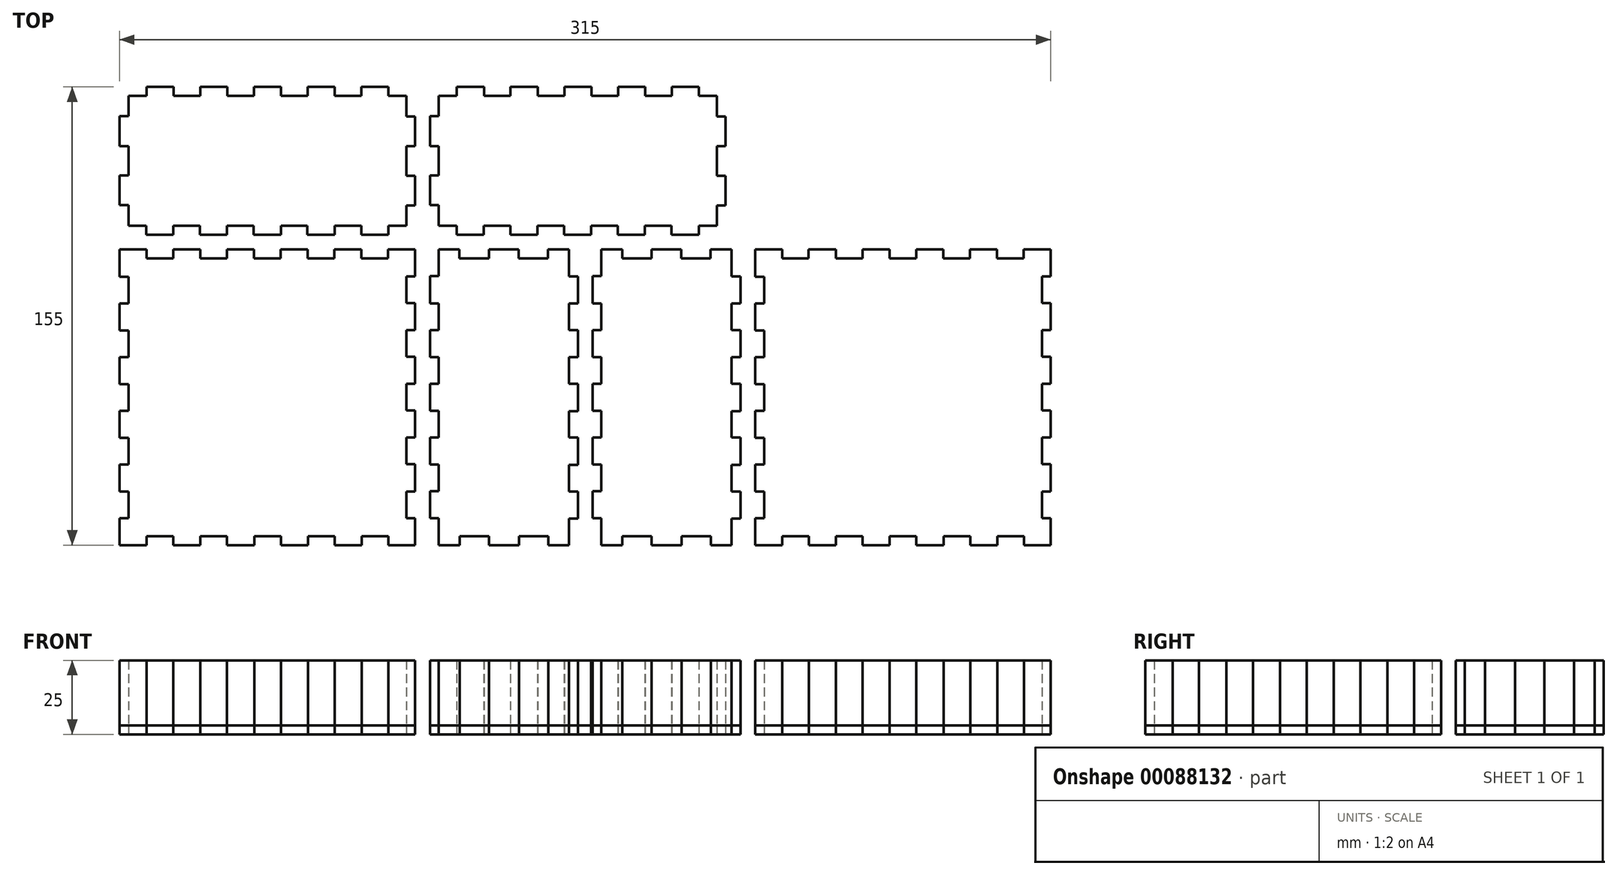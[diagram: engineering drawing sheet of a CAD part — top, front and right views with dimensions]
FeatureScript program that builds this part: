
annotation { "Feature Type Name" : "Feature", "Feature Type Description" : "" }
export const myFeature = defineFeature(function(context is Context, id is Id, definition is map)
    precondition{}
    {
        {
            var Q0;
            Q0=qCreatedBy(makeId("Top.planeOp"),FACE);
            var sketch = newSketch(context, id + "F0", { "sketchPlane" : qUnion([Q0])});
            skLineSegment(sketch, "E0", {"start": v(-154.5, -68.4) * mm, "end": v(-157.5, -68.4) * mm});
            skLineSegment(sketch, "E1", {"start": v(-157.5, -68.4) * mm, "end": v(-157.5, -77.5) * mm});
            skLineSegment(sketch, "E2", {"start": v(-157.5, -77.5) * mm, "end": v(-148.33, -77.5) * mm});
            skLineSegment(sketch, "E3", {"start": v(-148.33, -77.5) * mm, "end": v(-148.33, -74.5) * mm});
            skLineSegment(sketch, "E4", {"start": v(-148.33, -74.5) * mm, "end": v(-139.32, -74.5) * mm});
            skLineSegment(sketch, "E5", {"start": v(-139.32, -74.5) * mm, "end": v(-139.32, -77.5) * mm});
            skLineSegment(sketch, "E6", {"start": v(-139.32, -77.5) * mm, "end": v(-130.15, -77.5) * mm});
            skLineSegment(sketch, "E7", {"start": v(-130.15, -77.5) * mm, "end": v(-130.15, -74.5) * mm});
            skLineSegment(sketch, "E8", {"start": v(-130.15, -74.5) * mm, "end": v(-121.14, -74.5) * mm});
            skLineSegment(sketch, "E9", {"start": v(-121.14, -74.5) * mm, "end": v(-121.14, -77.5) * mm});
            skLineSegment(sketch, "E10", {"start": v(-121.14, -77.5) * mm, "end": v(-111.97, -77.5) * mm});
            skLineSegment(sketch, "E11", {"start": v(-111.97, -77.5) * mm, "end": v(-111.97, -74.5) * mm});
            skLineSegment(sketch, "E12", {"start": v(-111.97, -74.5) * mm, "end": v(-102.95, -74.5) * mm});
            skLineSegment(sketch, "E13", {"start": v(-102.95, -74.5) * mm, "end": v(-102.95, -77.5) * mm});
            skLineSegment(sketch, "E14", {"start": v(-102.95, -77.5) * mm, "end": v(-93.78, -77.5) * mm});
            skLineSegment(sketch, "E15", {"start": v(-93.78, -77.5) * mm, "end": v(-93.78, -74.5) * mm});
            skLineSegment(sketch, "E16", {"start": v(-93.78, -74.5) * mm, "end": v(-84.77, -74.5) * mm});
            skLineSegment(sketch, "E17", {"start": v(-84.77, -74.5) * mm, "end": v(-84.77, -77.5) * mm});
            skLineSegment(sketch, "E18", {"start": v(-84.77, -77.5) * mm, "end": v(-75.6, -77.5) * mm});
            skLineSegment(sketch, "E19", {"start": v(-75.6, -77.5) * mm, "end": v(-75.6, -74.5) * mm});
            skLineSegment(sketch, "E20", {"start": v(-75.6, -74.5) * mm, "end": v(-66.6, -74.5) * mm});
            skLineSegment(sketch, "E21", {"start": v(-66.6, -74.5) * mm, "end": v(-66.6, -77.5) * mm});
            skLineSegment(sketch, "E22", {"start": v(-66.6, -77.5) * mm, "end": v(-57.5, -77.5) * mm});
            skLineSegment(sketch, "E23", {"start": v(-57.5, -77.5) * mm, "end": v(-57.5, -68.33) * mm});
            skLineSegment(sketch, "E24", {"start": v(-57.5, -68.33) * mm, "end": v(-60.5, -68.33) * mm});
            skLineSegment(sketch, "E25", {"start": v(-60.5, -68.33) * mm, "end": v(-60.5, -59.32) * mm});
            skLineSegment(sketch, "E26", {"start": v(-60.5, -59.32) * mm, "end": v(-57.5, -59.32) * mm});
            skLineSegment(sketch, "E27", {"start": v(-57.5, -59.32) * mm, "end": v(-57.5, -50.15) * mm});
            skLineSegment(sketch, "E28", {"start": v(-57.5, -50.15) * mm, "end": v(-60.5, -50.15) * mm});
            skLineSegment(sketch, "E29", {"start": v(-60.5, -50.15) * mm, "end": v(-60.5, -41.14) * mm});
            skLineSegment(sketch, "E30", {"start": v(-60.5, -41.14) * mm, "end": v(-57.5, -41.14) * mm});
            skLineSegment(sketch, "E31", {"start": v(-57.5, -41.14) * mm, "end": v(-57.5, -31.97) * mm});
            skLineSegment(sketch, "E32", {"start": v(-57.5, -31.97) * mm, "end": v(-60.5, -31.97) * mm});
            skLineSegment(sketch, "E33", {"start": v(-60.5, -31.97) * mm, "end": v(-60.5, -22.95) * mm});
            skLineSegment(sketch, "E34", {"start": v(-60.5, -22.95) * mm, "end": v(-57.5, -22.95) * mm});
            skLineSegment(sketch, "E35", {"start": v(-57.5, -22.95) * mm, "end": v(-57.5, -13.78) * mm});
            skLineSegment(sketch, "E36", {"start": v(-57.5, -13.78) * mm, "end": v(-60.5, -13.78) * mm});
            skLineSegment(sketch, "E37", {"start": v(-60.5, -13.78) * mm, "end": v(-60.5, -4.77) * mm});
            skLineSegment(sketch, "E38", {"start": v(-60.5, -4.77) * mm, "end": v(-57.5, -4.77) * mm});
            skLineSegment(sketch, "E39", {"start": v(-57.5, -4.77) * mm, "end": v(-57.5, 4.4) * mm});
            skLineSegment(sketch, "E40", {"start": v(-57.5, 4.4) * mm, "end": v(-60.5, 4.4) * mm});
            skLineSegment(sketch, "E41", {"start": v(-60.5, 4.4) * mm, "end": v(-60.5, 13.4) * mm});
            skLineSegment(sketch, "E42", {"start": v(-60.5, 13.4) * mm, "end": v(-57.5, 13.4) * mm});
            skLineSegment(sketch, "E43", {"start": v(-57.5, 13.4) * mm, "end": v(-57.5, 22.5) * mm});
            skLineSegment(sketch, "E44", {"start": v(-57.5, 22.5) * mm, "end": v(-66.67, 22.5) * mm});
            skLineSegment(sketch, "E45", {"start": v(-66.67, 22.5) * mm, "end": v(-66.67, 19.5) * mm});
            skLineSegment(sketch, "E46", {"start": v(-66.67, 19.5) * mm, "end": v(-75.68, 19.5) * mm});
            skLineSegment(sketch, "E47", {"start": v(-75.68, 19.5) * mm, "end": v(-75.68, 22.5) * mm});
            skLineSegment(sketch, "E48", {"start": v(-75.68, 22.5) * mm, "end": v(-84.85, 22.5) * mm});
            skLineSegment(sketch, "E49", {"start": v(-84.85, 22.5) * mm, "end": v(-84.85, 19.5) * mm});
            skLineSegment(sketch, "E50", {"start": v(-84.85, 19.5) * mm, "end": v(-93.86, 19.5) * mm});
            skLineSegment(sketch, "E51", {"start": v(-93.86, 19.5) * mm, "end": v(-93.86, 22.5) * mm});
            skLineSegment(sketch, "E52", {"start": v(-93.86, 22.5) * mm, "end": v(-103.03, 22.5) * mm});
            skLineSegment(sketch, "E53", {"start": v(-103.03, 22.5) * mm, "end": v(-103.03, 19.5) * mm});
            skLineSegment(sketch, "E54", {"start": v(-103.03, 19.5) * mm, "end": v(-112.05, 19.5) * mm});
            skLineSegment(sketch, "E55", {"start": v(-112.05, 19.5) * mm, "end": v(-112.05, 22.5) * mm});
            skLineSegment(sketch, "E56", {"start": v(-112.05, 22.5) * mm, "end": v(-121.22, 22.5) * mm});
            skLineSegment(sketch, "E57", {"start": v(-121.22, 22.5) * mm, "end": v(-121.22, 19.5) * mm});
            skLineSegment(sketch, "E58", {"start": v(-121.22, 19.5) * mm, "end": v(-130.23, 19.5) * mm});
            skLineSegment(sketch, "E59", {"start": v(-130.23, 19.5) * mm, "end": v(-130.23, 22.5) * mm});
            skLineSegment(sketch, "E60", {"start": v(-130.23, 22.5) * mm, "end": v(-139.4, 22.5) * mm});
            skLineSegment(sketch, "E61", {"start": v(-139.4, 22.5) * mm, "end": v(-139.4, 19.5) * mm});
            skLineSegment(sketch, "E62", {"start": v(-139.4, 19.5) * mm, "end": v(-148.4, 19.5) * mm});
            skLineSegment(sketch, "E63", {"start": v(-148.4, 19.5) * mm, "end": v(-148.4, 22.5) * mm});
            skLineSegment(sketch, "E64", {"start": v(-148.4, 22.5) * mm, "end": v(-157.5, 22.5) * mm});
            skLineSegment(sketch, "E65", {"start": v(-157.5, 22.5) * mm, "end": v(-157.5, 13.33) * mm});
            skLineSegment(sketch, "E66", {"start": v(-157.5, 13.33) * mm, "end": v(-154.5, 13.33) * mm});
            skLineSegment(sketch, "E67", {"start": v(-154.5, 13.33) * mm, "end": v(-154.5, 4.32) * mm});
            skLineSegment(sketch, "E68", {"start": v(-154.5, 4.32) * mm, "end": v(-157.5, 4.32) * mm});
            skLineSegment(sketch, "E69", {"start": v(-157.5, 4.32) * mm, "end": v(-157.5, -4.85) * mm});
            skLineSegment(sketch, "E70", {"start": v(-157.5, -4.85) * mm, "end": v(-154.5, -4.85) * mm});
            skLineSegment(sketch, "E71", {"start": v(-154.5, -4.85) * mm, "end": v(-154.5, -13.86) * mm});
            skLineSegment(sketch, "E72", {"start": v(-154.5, -13.86) * mm, "end": v(-157.5, -13.86) * mm});
            skLineSegment(sketch, "E73", {"start": v(-157.5, -13.86) * mm, "end": v(-157.5, -23.03) * mm});
            skLineSegment(sketch, "E74", {"start": v(-157.5, -23.03) * mm, "end": v(-154.5, -23.03) * mm});
            skLineSegment(sketch, "E75", {"start": v(-154.5, -23.03) * mm, "end": v(-154.5, -32.05) * mm});
            skLineSegment(sketch, "E76", {"start": v(-154.5, -32.05) * mm, "end": v(-157.5, -32.05) * mm});
            skLineSegment(sketch, "E77", {"start": v(-157.5, -32.05) * mm, "end": v(-157.5, -41.22) * mm});
            skLineSegment(sketch, "E78", {"start": v(-157.5, -41.22) * mm, "end": v(-154.5, -41.22) * mm});
            skLineSegment(sketch, "E79", {"start": v(-154.5, -41.22) * mm, "end": v(-154.5, -50.23) * mm});
            skLineSegment(sketch, "E80", {"start": v(-154.5, -50.23) * mm, "end": v(-157.5, -50.23) * mm});
            skLineSegment(sketch, "E81", {"start": v(-157.5, -50.23) * mm, "end": v(-157.5, -59.4) * mm});
            skLineSegment(sketch, "E82", {"start": v(-157.5, -59.4) * mm, "end": v(-154.5, -59.4) * mm});
            skLineSegment(sketch, "E83", {"start": v(-154.5, -59.4) * mm, "end": v(-154.5, -68.4) * mm});
            skLineSegment(sketch, "E84", {"start": v(60.5, -68.4) * mm, "end": v(57.5, -68.4) * mm});
            skLineSegment(sketch, "E85", {"start": v(57.5, -68.4) * mm, "end": v(57.5, -77.5) * mm});
            skLineSegment(sketch, "E86", {"start": v(57.5, -77.5) * mm, "end": v(66.67, -77.5) * mm});
            skLineSegment(sketch, "E87", {"start": v(66.67, -77.5) * mm, "end": v(66.67, -74.5) * mm});
            skLineSegment(sketch, "E88", {"start": v(66.67, -74.5) * mm, "end": v(75.68, -74.5) * mm});
            skLineSegment(sketch, "E89", {"start": v(75.68, -74.5) * mm, "end": v(75.68, -77.5) * mm});
            skLineSegment(sketch, "E90", {"start": v(75.68, -77.5) * mm, "end": v(84.85, -77.5) * mm});
            skLineSegment(sketch, "E91", {"start": v(84.85, -77.5) * mm, "end": v(84.85, -74.5) * mm});
            skLineSegment(sketch, "E92", {"start": v(84.85, -74.5) * mm, "end": v(93.86, -74.5) * mm});
            skLineSegment(sketch, "E93", {"start": v(93.86, -74.5) * mm, "end": v(93.86, -77.5) * mm});
            skLineSegment(sketch, "E94", {"start": v(93.86, -77.5) * mm, "end": v(103.03, -77.5) * mm});
            skLineSegment(sketch, "E95", {"start": v(103.03, -77.5) * mm, "end": v(103.03, -74.5) * mm});
            skLineSegment(sketch, "E96", {"start": v(103.03, -74.5) * mm, "end": v(112.05, -74.5) * mm});
            skLineSegment(sketch, "E97", {"start": v(112.05, -74.5) * mm, "end": v(112.05, -77.5) * mm});
            skLineSegment(sketch, "E98", {"start": v(112.05, -77.5) * mm, "end": v(121.22, -77.5) * mm});
            skLineSegment(sketch, "E99", {"start": v(121.22, -77.5) * mm, "end": v(121.22, -74.5) * mm});
            skLineSegment(sketch, "E100", {"start": v(121.22, -74.5) * mm, "end": v(130.23, -74.5) * mm});
            skLineSegment(sketch, "E101", {"start": v(130.23, -74.5) * mm, "end": v(130.23, -77.5) * mm});
            skLineSegment(sketch, "E102", {"start": v(130.23, -77.5) * mm, "end": v(139.4, -77.5) * mm});
            skLineSegment(sketch, "E103", {"start": v(139.4, -77.5) * mm, "end": v(139.4, -74.5) * mm});
            skLineSegment(sketch, "E104", {"start": v(139.4, -74.5) * mm, "end": v(148.4, -74.5) * mm});
            skLineSegment(sketch, "E105", {"start": v(148.4, -74.5) * mm, "end": v(148.4, -77.5) * mm});
            skLineSegment(sketch, "E106", {"start": v(148.4, -77.5) * mm, "end": v(157.5, -77.5) * mm});
            skLineSegment(sketch, "E107", {"start": v(157.5, -77.5) * mm, "end": v(157.5, -68.33) * mm});
            skLineSegment(sketch, "E108", {"start": v(157.5, -68.33) * mm, "end": v(154.5, -68.33) * mm});
            skLineSegment(sketch, "E109", {"start": v(154.5, -68.33) * mm, "end": v(154.5, -59.32) * mm});
            skLineSegment(sketch, "E110", {"start": v(154.5, -59.32) * mm, "end": v(157.5, -59.32) * mm});
            skLineSegment(sketch, "E111", {"start": v(157.5, -59.32) * mm, "end": v(157.5, -50.15) * mm});
            skLineSegment(sketch, "E112", {"start": v(157.5, -50.15) * mm, "end": v(154.5, -50.15) * mm});
            skLineSegment(sketch, "E113", {"start": v(154.5, -50.15) * mm, "end": v(154.5, -41.14) * mm});
            skLineSegment(sketch, "E114", {"start": v(154.5, -41.14) * mm, "end": v(157.5, -41.14) * mm});
            skLineSegment(sketch, "E115", {"start": v(157.5, -41.14) * mm, "end": v(157.5, -31.97) * mm});
            skLineSegment(sketch, "E116", {"start": v(157.5, -31.97) * mm, "end": v(154.5, -31.97) * mm});
            skLineSegment(sketch, "E117", {"start": v(154.5, -31.97) * mm, "end": v(154.5, -22.95) * mm});
            skLineSegment(sketch, "E118", {"start": v(154.5, -22.95) * mm, "end": v(157.5, -22.95) * mm});
            skLineSegment(sketch, "E119", {"start": v(157.5, -22.95) * mm, "end": v(157.5, -13.78) * mm});
            skLineSegment(sketch, "E120", {"start": v(157.5, -13.78) * mm, "end": v(154.5, -13.78) * mm});
            skLineSegment(sketch, "E121", {"start": v(154.5, -13.78) * mm, "end": v(154.5, -4.77) * mm});
            skLineSegment(sketch, "E122", {"start": v(154.5, -4.77) * mm, "end": v(157.5, -4.77) * mm});
            skLineSegment(sketch, "E123", {"start": v(157.5, -4.77) * mm, "end": v(157.5, 4.4) * mm});
            skLineSegment(sketch, "E124", {"start": v(157.5, 4.4) * mm, "end": v(154.5, 4.4) * mm});
            skLineSegment(sketch, "E125", {"start": v(154.5, 4.4) * mm, "end": v(154.5, 13.4) * mm});
            skLineSegment(sketch, "E126", {"start": v(154.5, 13.4) * mm, "end": v(157.5, 13.4) * mm});
            skLineSegment(sketch, "E127", {"start": v(157.5, 13.4) * mm, "end": v(157.5, 22.5) * mm});
            skLineSegment(sketch, "E128", {"start": v(157.5, 22.5) * mm, "end": v(148.33, 22.5) * mm});
            skLineSegment(sketch, "E129", {"start": v(148.33, 22.5) * mm, "end": v(148.33, 19.5) * mm});
            skLineSegment(sketch, "E130", {"start": v(148.33, 19.5) * mm, "end": v(139.32, 19.5) * mm});
            skLineSegment(sketch, "E131", {"start": v(139.32, 19.5) * mm, "end": v(139.32, 22.5) * mm});
            skLineSegment(sketch, "E132", {"start": v(139.32, 22.5) * mm, "end": v(130.15, 22.5) * mm});
            skLineSegment(sketch, "E133", {"start": v(130.15, 22.5) * mm, "end": v(130.15, 19.5) * mm});
            skLineSegment(sketch, "E134", {"start": v(130.15, 19.5) * mm, "end": v(121.14, 19.5) * mm});
            skLineSegment(sketch, "E135", {"start": v(121.14, 19.5) * mm, "end": v(121.14, 22.5) * mm});
            skLineSegment(sketch, "E136", {"start": v(121.14, 22.5) * mm, "end": v(111.97, 22.5) * mm});
            skLineSegment(sketch, "E137", {"start": v(111.97, 22.5) * mm, "end": v(111.97, 19.5) * mm});
            skLineSegment(sketch, "E138", {"start": v(111.97, 19.5) * mm, "end": v(102.95, 19.5) * mm});
            skLineSegment(sketch, "E139", {"start": v(102.95, 19.5) * mm, "end": v(102.95, 22.5) * mm});
            skLineSegment(sketch, "E140", {"start": v(102.95, 22.5) * mm, "end": v(93.78, 22.5) * mm});
            skLineSegment(sketch, "E141", {"start": v(93.78, 22.5) * mm, "end": v(93.78, 19.5) * mm});
            skLineSegment(sketch, "E142", {"start": v(93.78, 19.5) * mm, "end": v(84.77, 19.5) * mm});
            skLineSegment(sketch, "E143", {"start": v(84.77, 19.5) * mm, "end": v(84.77, 22.5) * mm});
            skLineSegment(sketch, "E144", {"start": v(84.77, 22.5) * mm, "end": v(75.6, 22.5) * mm});
            skLineSegment(sketch, "E145", {"start": v(75.6, 22.5) * mm, "end": v(75.6, 19.5) * mm});
            skLineSegment(sketch, "E146", {"start": v(75.6, 19.5) * mm, "end": v(66.6, 19.5) * mm});
            skLineSegment(sketch, "E147", {"start": v(66.6, 19.5) * mm, "end": v(66.6, 22.5) * mm});
            skLineSegment(sketch, "E148", {"start": v(66.6, 22.5) * mm, "end": v(57.5, 22.5) * mm});
            skLineSegment(sketch, "E149", {"start": v(57.5, 22.5) * mm, "end": v(57.5, 13.33) * mm});
            skLineSegment(sketch, "E150", {"start": v(57.5, 13.33) * mm, "end": v(60.5, 13.33) * mm});
            skLineSegment(sketch, "E151", {"start": v(60.5, 13.33) * mm, "end": v(60.5, 4.32) * mm});
            skLineSegment(sketch, "E152", {"start": v(60.5, 4.32) * mm, "end": v(57.5, 4.32) * mm});
            skLineSegment(sketch, "E153", {"start": v(57.5, 4.32) * mm, "end": v(57.5, -4.85) * mm});
            skLineSegment(sketch, "E154", {"start": v(57.5, -4.85) * mm, "end": v(60.5, -4.85) * mm});
            skLineSegment(sketch, "E155", {"start": v(60.5, -4.85) * mm, "end": v(60.5, -13.86) * mm});
            skLineSegment(sketch, "E156", {"start": v(60.5, -13.86) * mm, "end": v(57.5, -13.86) * mm});
            skLineSegment(sketch, "E157", {"start": v(57.5, -13.86) * mm, "end": v(57.5, -23.03) * mm});
            skLineSegment(sketch, "E158", {"start": v(57.5, -23.03) * mm, "end": v(60.5, -23.03) * mm});
            skLineSegment(sketch, "E159", {"start": v(60.5, -23.03) * mm, "end": v(60.5, -32.05) * mm});
            skLineSegment(sketch, "E160", {"start": v(60.5, -32.05) * mm, "end": v(57.5, -32.05) * mm});
            skLineSegment(sketch, "E161", {"start": v(57.5, -32.05) * mm, "end": v(57.5, -41.22) * mm});
            skLineSegment(sketch, "E162", {"start": v(57.5, -41.22) * mm, "end": v(60.5, -41.22) * mm});
            skLineSegment(sketch, "E163", {"start": v(60.5, -41.22) * mm, "end": v(60.5, -50.23) * mm});
            skLineSegment(sketch, "E164", {"start": v(60.5, -50.23) * mm, "end": v(57.5, -50.23) * mm});
            skLineSegment(sketch, "E165", {"start": v(57.5, -50.23) * mm, "end": v(57.5, -59.4) * mm});
            skLineSegment(sketch, "E166", {"start": v(57.5, -59.4) * mm, "end": v(60.5, -59.4) * mm});
            skLineSegment(sketch, "E167", {"start": v(60.5, -59.4) * mm, "end": v(60.5, -68.4) * mm});
            skLineSegment(sketch, "E168", {"start": v(-157.5, 47.58) * mm, "end": v(-157.5, 37.5) * mm});
            skLineSegment(sketch, "E169", {"start": v(-157.5, 37.5) * mm, "end": v(-154.5, 37.5) * mm});
            skLineSegment(sketch, "E170", {"start": v(-154.5, 37.5) * mm, "end": v(-154.5, 30.5) * mm});
            skLineSegment(sketch, "E171", {"start": v(-154.5, 30.5) * mm, "end": v(-148.49, 30.5) * mm});
            skLineSegment(sketch, "E172", {"start": v(-148.49, 30.5) * mm, "end": v(-148.49, 27.5) * mm});
            skLineSegment(sketch, "E173", {"start": v(-148.49, 27.5) * mm, "end": v(-139.32, 27.5) * mm});
            skLineSegment(sketch, "E174", {"start": v(-139.32, 27.5) * mm, "end": v(-139.32, 30.5) * mm});
            skLineSegment(sketch, "E175", {"start": v(-139.32, 30.5) * mm, "end": v(-130.3, 30.5) * mm});
            skLineSegment(sketch, "E176", {"start": v(-130.3, 30.5) * mm, "end": v(-130.3, 27.5) * mm});
            skLineSegment(sketch, "E177", {"start": v(-130.3, 27.5) * mm, "end": v(-121.14, 27.5) * mm});
            skLineSegment(sketch, "E178", {"start": v(-121.14, 27.5) * mm, "end": v(-121.14, 30.5) * mm});
            skLineSegment(sketch, "E179", {"start": v(-121.14, 30.5) * mm, "end": v(-112.13, 30.5) * mm});
            skLineSegment(sketch, "E180", {"start": v(-112.13, 30.5) * mm, "end": v(-112.13, 27.5) * mm});
            skLineSegment(sketch, "E181", {"start": v(-112.13, 27.5) * mm, "end": v(-102.95, 27.5) * mm});
            skLineSegment(sketch, "E182", {"start": v(-102.95, 27.5) * mm, "end": v(-102.95, 30.5) * mm});
            skLineSegment(sketch, "E183", {"start": v(-102.95, 30.5) * mm, "end": v(-93.94, 30.5) * mm});
            skLineSegment(sketch, "E184", {"start": v(-93.94, 30.5) * mm, "end": v(-93.94, 27.5) * mm});
            skLineSegment(sketch, "E185", {"start": v(-93.94, 27.5) * mm, "end": v(-84.77, 27.5) * mm});
            skLineSegment(sketch, "E186", {"start": v(-84.77, 27.5) * mm, "end": v(-84.77, 30.5) * mm});
            skLineSegment(sketch, "E187", {"start": v(-84.77, 30.5) * mm, "end": v(-75.76, 30.5) * mm});
            skLineSegment(sketch, "E188", {"start": v(-75.76, 30.5) * mm, "end": v(-75.76, 27.5) * mm});
            skLineSegment(sketch, "E189", {"start": v(-75.76, 27.5) * mm, "end": v(-66.6, 27.5) * mm});
            skLineSegment(sketch, "E190", {"start": v(-66.6, 27.5) * mm, "end": v(-66.6, 30.5) * mm});
            skLineSegment(sketch, "E191", {"start": v(-66.6, 30.5) * mm, "end": v(-60.5, 30.5) * mm});
            skLineSegment(sketch, "E192", {"start": v(-60.5, 30.5) * mm, "end": v(-60.5, 37.42) * mm});
            skLineSegment(sketch, "E193", {"start": v(-60.5, 37.42) * mm, "end": v(-57.5, 37.42) * mm});
            skLineSegment(sketch, "E194", {"start": v(-57.5, 37.42) * mm, "end": v(-57.5, 47.5) * mm});
            skLineSegment(sketch, "E195", {"start": v(-57.5, 47.5) * mm, "end": v(-60.5, 47.5) * mm});
            skLineSegment(sketch, "E196", {"start": v(-60.5, 47.5) * mm, "end": v(-60.5, 57.42) * mm});
            skLineSegment(sketch, "E197", {"start": v(-60.5, 57.42) * mm, "end": v(-57.5, 57.42) * mm});
            skLineSegment(sketch, "E198", {"start": v(-57.5, 57.42) * mm, "end": v(-57.5, 67.5) * mm});
            skLineSegment(sketch, "E199", {"start": v(-57.5, 67.5) * mm, "end": v(-60.5, 67.5) * mm});
            skLineSegment(sketch, "E200", {"start": v(-60.5, 67.5) * mm, "end": v(-60.5, 74.5) * mm});
            skLineSegment(sketch, "E201", {"start": v(-60.5, 74.5) * mm, "end": v(-66.51, 74.5) * mm});
            skLineSegment(sketch, "E202", {"start": v(-66.51, 74.5) * mm, "end": v(-66.51, 77.5) * mm});
            skLineSegment(sketch, "E203", {"start": v(-66.51, 77.5) * mm, "end": v(-75.68, 77.5) * mm});
            skLineSegment(sketch, "E204", {"start": v(-75.68, 77.5) * mm, "end": v(-75.68, 74.5) * mm});
            skLineSegment(sketch, "E205", {"start": v(-75.68, 74.5) * mm, "end": v(-84.7, 74.5) * mm});
            skLineSegment(sketch, "E206", {"start": v(-84.7, 74.5) * mm, "end": v(-84.7, 77.5) * mm});
            skLineSegment(sketch, "E207", {"start": v(-84.7, 77.5) * mm, "end": v(-93.86, 77.5) * mm});
            skLineSegment(sketch, "E208", {"start": v(-93.86, 77.5) * mm, "end": v(-93.86, 74.5) * mm});
            skLineSegment(sketch, "E209", {"start": v(-93.86, 74.5) * mm, "end": v(-102.87, 74.5) * mm});
            skLineSegment(sketch, "E210", {"start": v(-102.87, 74.5) * mm, "end": v(-102.87, 77.5) * mm});
            skLineSegment(sketch, "E211", {"start": v(-102.87, 77.5) * mm, "end": v(-112.05, 77.5) * mm});
            skLineSegment(sketch, "E212", {"start": v(-112.05, 77.5) * mm, "end": v(-112.05, 74.5) * mm});
            skLineSegment(sketch, "E213", {"start": v(-112.05, 74.5) * mm, "end": v(-121.06, 74.5) * mm});
            skLineSegment(sketch, "E214", {"start": v(-121.06, 74.5) * mm, "end": v(-121.06, 77.5) * mm});
            skLineSegment(sketch, "E215", {"start": v(-121.06, 77.5) * mm, "end": v(-130.23, 77.5) * mm});
            skLineSegment(sketch, "E216", {"start": v(-130.23, 77.5) * mm, "end": v(-130.23, 74.5) * mm});
            skLineSegment(sketch, "E217", {"start": v(-130.23, 74.5) * mm, "end": v(-139.24, 74.5) * mm});
            skLineSegment(sketch, "E218", {"start": v(-139.24, 74.5) * mm, "end": v(-139.24, 77.5) * mm});
            skLineSegment(sketch, "E219", {"start": v(-139.24, 77.5) * mm, "end": v(-148.4, 77.5) * mm});
            skLineSegment(sketch, "E220", {"start": v(-148.4, 77.5) * mm, "end": v(-148.4, 74.5) * mm});
            skLineSegment(sketch, "E221", {"start": v(-148.4, 74.5) * mm, "end": v(-154.5, 74.5) * mm});
            skLineSegment(sketch, "E222", {"start": v(-154.5, 74.5) * mm, "end": v(-154.5, 67.58) * mm});
            skLineSegment(sketch, "E223", {"start": v(-154.5, 67.58) * mm, "end": v(-157.5, 67.58) * mm});
            skLineSegment(sketch, "E224", {"start": v(-157.5, 67.58) * mm, "end": v(-157.5, 57.5) * mm});
            skLineSegment(sketch, "E225", {"start": v(-157.5, 57.5) * mm, "end": v(-154.5, 57.5) * mm});
            skLineSegment(sketch, "E226", {"start": v(-154.5, 57.5) * mm, "end": v(-154.5, 47.58) * mm});
            skLineSegment(sketch, "E227", {"start": v(-154.5, 47.58) * mm, "end": v(-157.5, 47.58) * mm});
            skLineSegment(sketch, "E228", {"start": v(-49.5, -77.5) * mm, "end": v(-42.42, -77.5) * mm});
            skLineSegment(sketch, "E229", {"start": v(-42.42, -77.5) * mm, "end": v(-42.42, -74.5) * mm});
            skLineSegment(sketch, "E230", {"start": v(-42.42, -74.5) * mm, "end": v(-32.5, -74.5) * mm});
            skLineSegment(sketch, "E231", {"start": v(-32.5, -74.5) * mm, "end": v(-32.5, -77.5) * mm});
            skLineSegment(sketch, "E232", {"start": v(-32.5, -77.5) * mm, "end": v(-22.42, -77.5) * mm});
            skLineSegment(sketch, "E233", {"start": v(-22.42, -77.5) * mm, "end": v(-22.42, -74.5) * mm});
            skLineSegment(sketch, "E234", {"start": v(-22.42, -74.5) * mm, "end": v(-12.5, -74.5) * mm});
            skLineSegment(sketch, "E235", {"start": v(-12.5, -74.5) * mm, "end": v(-12.5, -77.5) * mm});
            skLineSegment(sketch, "E236", {"start": v(-12.5, -77.5) * mm, "end": v(-5.5, -77.5) * mm});
            skLineSegment(sketch, "E237", {"start": v(-5.5, -77.5) * mm, "end": v(-5.5, -68.49) * mm});
            skLineSegment(sketch, "E238", {"start": v(-5.5, -68.49) * mm, "end": v(-2.5, -68.49) * mm});
            skLineSegment(sketch, "E239", {"start": v(-2.5, -68.49) * mm, "end": v(-2.5, -59.32) * mm});
            skLineSegment(sketch, "E240", {"start": v(-2.5, -59.32) * mm, "end": v(-5.5, -59.32) * mm});
            skLineSegment(sketch, "E241", {"start": v(-5.5, -59.32) * mm, "end": v(-5.5, -50.3) * mm});
            skLineSegment(sketch, "E242", {"start": v(-5.5, -50.3) * mm, "end": v(-2.5, -50.3) * mm});
            skLineSegment(sketch, "E243", {"start": v(-2.5, -50.3) * mm, "end": v(-2.5, -41.14) * mm});
            skLineSegment(sketch, "E244", {"start": v(-2.5, -41.14) * mm, "end": v(-5.5, -41.14) * mm});
            skLineSegment(sketch, "E245", {"start": v(-5.5, -41.14) * mm, "end": v(-5.5, -32.13) * mm});
            skLineSegment(sketch, "E246", {"start": v(-5.5, -32.13) * mm, "end": v(-2.5, -32.13) * mm});
            skLineSegment(sketch, "E247", {"start": v(-2.5, -32.13) * mm, "end": v(-2.5, -22.95) * mm});
            skLineSegment(sketch, "E248", {"start": v(-2.5, -22.95) * mm, "end": v(-5.5, -22.95) * mm});
            skLineSegment(sketch, "E249", {"start": v(-5.5, -22.95) * mm, "end": v(-5.5, -13.94) * mm});
            skLineSegment(sketch, "E250", {"start": v(-5.5, -13.94) * mm, "end": v(-2.5, -13.94) * mm});
            skLineSegment(sketch, "E251", {"start": v(-2.5, -13.94) * mm, "end": v(-2.5, -4.77) * mm});
            skLineSegment(sketch, "E252", {"start": v(-2.5, -4.77) * mm, "end": v(-5.5, -4.77) * mm});
            skLineSegment(sketch, "E253", {"start": v(-5.5, -4.77) * mm, "end": v(-5.5, 4.24) * mm});
            skLineSegment(sketch, "E254", {"start": v(-5.5, 4.24) * mm, "end": v(-2.5, 4.24) * mm});
            skLineSegment(sketch, "E255", {"start": v(-2.5, 4.24) * mm, "end": v(-2.5, 13.4) * mm});
            skLineSegment(sketch, "E256", {"start": v(-2.5, 13.4) * mm, "end": v(-5.5, 13.4) * mm});
            skLineSegment(sketch, "E257", {"start": v(-5.5, 13.4) * mm, "end": v(-5.5, 22.5) * mm});
            skLineSegment(sketch, "E258", {"start": v(-5.5, 22.5) * mm, "end": v(-12.58, 22.5) * mm});
            skLineSegment(sketch, "E259", {"start": v(-12.58, 22.5) * mm, "end": v(-12.58, 19.5) * mm});
            skLineSegment(sketch, "E260", {"start": v(-12.58, 19.5) * mm, "end": v(-22.5, 19.5) * mm});
            skLineSegment(sketch, "E261", {"start": v(-22.5, 19.5) * mm, "end": v(-22.5, 22.5) * mm});
            skLineSegment(sketch, "E262", {"start": v(-22.5, 22.5) * mm, "end": v(-32.58, 22.5) * mm});
            skLineSegment(sketch, "E263", {"start": v(-32.58, 22.5) * mm, "end": v(-32.58, 19.5) * mm});
            skLineSegment(sketch, "E264", {"start": v(-32.58, 19.5) * mm, "end": v(-42.5, 19.5) * mm});
            skLineSegment(sketch, "E265", {"start": v(-42.5, 19.5) * mm, "end": v(-42.5, 22.5) * mm});
            skLineSegment(sketch, "E266", {"start": v(-42.5, 22.5) * mm, "end": v(-49.5, 22.5) * mm});
            skLineSegment(sketch, "E267", {"start": v(-49.5, 22.5) * mm, "end": v(-49.5, 13.49) * mm});
            skLineSegment(sketch, "E268", {"start": v(-49.5, 13.49) * mm, "end": v(-52.5, 13.49) * mm});
            skLineSegment(sketch, "E269", {"start": v(-52.5, 13.49) * mm, "end": v(-52.5, 4.32) * mm});
            skLineSegment(sketch, "E270", {"start": v(-52.5, 4.32) * mm, "end": v(-49.5, 4.32) * mm});
            skLineSegment(sketch, "E271", {"start": v(-49.5, 4.32) * mm, "end": v(-49.5, -4.7) * mm});
            skLineSegment(sketch, "E272", {"start": v(-49.5, -4.7) * mm, "end": v(-52.5, -4.7) * mm});
            skLineSegment(sketch, "E273", {"start": v(-52.5, -4.7) * mm, "end": v(-52.5, -13.86) * mm});
            skLineSegment(sketch, "E274", {"start": v(-52.5, -13.86) * mm, "end": v(-49.5, -13.86) * mm});
            skLineSegment(sketch, "E275", {"start": v(-49.5, -13.86) * mm, "end": v(-49.5, -22.87) * mm});
            skLineSegment(sketch, "E276", {"start": v(-49.5, -22.87) * mm, "end": v(-52.5, -22.87) * mm});
            skLineSegment(sketch, "E277", {"start": v(-52.5, -22.87) * mm, "end": v(-52.5, -32.05) * mm});
            skLineSegment(sketch, "E278", {"start": v(-52.5, -32.05) * mm, "end": v(-49.5, -32.05) * mm});
            skLineSegment(sketch, "E279", {"start": v(-49.5, -32.05) * mm, "end": v(-49.5, -41.06) * mm});
            skLineSegment(sketch, "E280", {"start": v(-49.5, -41.06) * mm, "end": v(-52.5, -41.06) * mm});
            skLineSegment(sketch, "E281", {"start": v(-52.5, -41.06) * mm, "end": v(-52.5, -50.23) * mm});
            skLineSegment(sketch, "E282", {"start": v(-52.5, -50.23) * mm, "end": v(-49.5, -50.23) * mm});
            skLineSegment(sketch, "E283", {"start": v(-49.5, -50.23) * mm, "end": v(-49.5, -59.24) * mm});
            skLineSegment(sketch, "E284", {"start": v(-49.5, -59.24) * mm, "end": v(-52.5, -59.24) * mm});
            skLineSegment(sketch, "E285", {"start": v(-52.5, -59.24) * mm, "end": v(-52.5, -68.4) * mm});
            skLineSegment(sketch, "E286", {"start": v(-52.5, -68.4) * mm, "end": v(-49.5, -68.4) * mm});
            skLineSegment(sketch, "E287", {"start": v(-49.5, -68.4) * mm, "end": v(-49.5, -77.5) * mm});
            skLineSegment(sketch, "E288", {"start": v(5.5, -77.5) * mm, "end": v(12.58, -77.5) * mm});
            skLineSegment(sketch, "E289", {"start": v(12.58, -77.5) * mm, "end": v(12.58, -74.5) * mm});
            skLineSegment(sketch, "E290", {"start": v(12.58, -74.5) * mm, "end": v(22.5, -74.5) * mm});
            skLineSegment(sketch, "E291", {"start": v(22.5, -74.5) * mm, "end": v(22.5, -77.5) * mm});
            skLineSegment(sketch, "E292", {"start": v(22.5, -77.5) * mm, "end": v(32.58, -77.5) * mm});
            skLineSegment(sketch, "E293", {"start": v(32.58, -77.5) * mm, "end": v(32.58, -74.5) * mm});
            skLineSegment(sketch, "E294", {"start": v(32.58, -74.5) * mm, "end": v(42.5, -74.5) * mm});
            skLineSegment(sketch, "E295", {"start": v(42.5, -74.5) * mm, "end": v(42.5, -77.5) * mm});
            skLineSegment(sketch, "E296", {"start": v(42.5, -77.5) * mm, "end": v(49.5, -77.5) * mm});
            skLineSegment(sketch, "E297", {"start": v(49.5, -77.5) * mm, "end": v(49.5, -68.49) * mm});
            skLineSegment(sketch, "E298", {"start": v(49.5, -68.49) * mm, "end": v(52.5, -68.49) * mm});
            skLineSegment(sketch, "E299", {"start": v(52.5, -68.49) * mm, "end": v(52.5, -59.32) * mm});
            skLineSegment(sketch, "E300", {"start": v(52.5, -59.32) * mm, "end": v(49.5, -59.32) * mm});
            skLineSegment(sketch, "E301", {"start": v(49.5, -59.32) * mm, "end": v(49.5, -50.3) * mm});
            skLineSegment(sketch, "E302", {"start": v(49.5, -50.3) * mm, "end": v(52.5, -50.3) * mm});
            skLineSegment(sketch, "E303", {"start": v(52.5, -50.3) * mm, "end": v(52.5, -41.14) * mm});
            skLineSegment(sketch, "E304", {"start": v(52.5, -41.14) * mm, "end": v(49.5, -41.14) * mm});
            skLineSegment(sketch, "E305", {"start": v(49.5, -41.14) * mm, "end": v(49.5, -32.13) * mm});
            skLineSegment(sketch, "E306", {"start": v(49.5, -32.13) * mm, "end": v(52.5, -32.13) * mm});
            skLineSegment(sketch, "E307", {"start": v(52.5, -32.13) * mm, "end": v(52.5, -22.95) * mm});
            skLineSegment(sketch, "E308", {"start": v(52.5, -22.95) * mm, "end": v(49.5, -22.95) * mm});
            skLineSegment(sketch, "E309", {"start": v(49.5, -22.95) * mm, "end": v(49.5, -13.94) * mm});
            skLineSegment(sketch, "E310", {"start": v(49.5, -13.94) * mm, "end": v(52.5, -13.94) * mm});
            skLineSegment(sketch, "E311", {"start": v(52.5, -13.94) * mm, "end": v(52.5, -4.77) * mm});
            skLineSegment(sketch, "E312", {"start": v(52.5, -4.77) * mm, "end": v(49.5, -4.77) * mm});
            skLineSegment(sketch, "E313", {"start": v(49.5, -4.77) * mm, "end": v(49.5, 4.24) * mm});
            skLineSegment(sketch, "E314", {"start": v(49.5, 4.24) * mm, "end": v(52.5, 4.24) * mm});
            skLineSegment(sketch, "E315", {"start": v(52.5, 4.24) * mm, "end": v(52.5, 13.4) * mm});
            skLineSegment(sketch, "E316", {"start": v(52.5, 13.4) * mm, "end": v(49.5, 13.4) * mm});
            skLineSegment(sketch, "E317", {"start": v(49.5, 13.4) * mm, "end": v(49.5, 22.5) * mm});
            skLineSegment(sketch, "E318", {"start": v(49.5, 22.5) * mm, "end": v(42.42, 22.5) * mm});
            skLineSegment(sketch, "E319", {"start": v(42.42, 22.5) * mm, "end": v(42.42, 19.5) * mm});
            skLineSegment(sketch, "E320", {"start": v(42.42, 19.5) * mm, "end": v(32.5, 19.5) * mm});
            skLineSegment(sketch, "E321", {"start": v(32.5, 19.5) * mm, "end": v(32.5, 22.5) * mm});
            skLineSegment(sketch, "E322", {"start": v(32.5, 22.5) * mm, "end": v(22.42, 22.5) * mm});
            skLineSegment(sketch, "E323", {"start": v(22.42, 22.5) * mm, "end": v(22.42, 19.5) * mm});
            skLineSegment(sketch, "E324", {"start": v(22.42, 19.5) * mm, "end": v(12.5, 19.5) * mm});
            skLineSegment(sketch, "E325", {"start": v(12.5, 19.5) * mm, "end": v(12.5, 22.5) * mm});
            skLineSegment(sketch, "E326", {"start": v(12.5, 22.5) * mm, "end": v(5.5, 22.5) * mm});
            skLineSegment(sketch, "E327", {"start": v(5.5, 22.5) * mm, "end": v(5.5, 13.49) * mm});
            skLineSegment(sketch, "E328", {"start": v(5.5, 13.49) * mm, "end": v(2.5, 13.49) * mm});
            skLineSegment(sketch, "E329", {"start": v(2.5, 13.49) * mm, "end": v(2.5, 4.32) * mm});
            skLineSegment(sketch, "E330", {"start": v(2.5, 4.32) * mm, "end": v(5.5, 4.32) * mm});
            skLineSegment(sketch, "E331", {"start": v(5.5, 4.32) * mm, "end": v(5.5, -4.7) * mm});
            skLineSegment(sketch, "E332", {"start": v(5.5, -4.7) * mm, "end": v(2.5, -4.7) * mm});
            skLineSegment(sketch, "E333", {"start": v(2.5, -4.7) * mm, "end": v(2.5, -13.86) * mm});
            skLineSegment(sketch, "E334", {"start": v(2.5, -13.86) * mm, "end": v(5.5, -13.86) * mm});
            skLineSegment(sketch, "E335", {"start": v(5.5, -13.86) * mm, "end": v(5.5, -22.87) * mm});
            skLineSegment(sketch, "E336", {"start": v(5.5, -22.87) * mm, "end": v(2.5, -22.87) * mm});
            skLineSegment(sketch, "E337", {"start": v(2.5, -22.87) * mm, "end": v(2.5, -32.05) * mm});
            skLineSegment(sketch, "E338", {"start": v(2.5, -32.05) * mm, "end": v(5.5, -32.05) * mm});
            skLineSegment(sketch, "E339", {"start": v(5.5, -32.05) * mm, "end": v(5.5, -41.06) * mm});
            skLineSegment(sketch, "E340", {"start": v(5.5, -41.06) * mm, "end": v(2.5, -41.06) * mm});
            skLineSegment(sketch, "E341", {"start": v(2.5, -41.06) * mm, "end": v(2.5, -50.23) * mm});
            skLineSegment(sketch, "E342", {"start": v(2.5, -50.23) * mm, "end": v(5.5, -50.23) * mm});
            skLineSegment(sketch, "E343", {"start": v(5.5, -50.23) * mm, "end": v(5.5, -59.24) * mm});
            skLineSegment(sketch, "E344", {"start": v(5.5, -59.24) * mm, "end": v(2.5, -59.24) * mm});
            skLineSegment(sketch, "E345", {"start": v(2.5, -59.24) * mm, "end": v(2.5, -68.4) * mm});
            skLineSegment(sketch, "E346", {"start": v(2.5, -68.4) * mm, "end": v(5.5, -68.4) * mm});
            skLineSegment(sketch, "E347", {"start": v(5.5, -68.4) * mm, "end": v(5.5, -77.5) * mm});
            skLineSegment(sketch, "E348", {"start": v(-52.5, 47.58) * mm, "end": v(-52.5, 37.5) * mm});
            skLineSegment(sketch, "E349", {"start": v(-52.5, 37.5) * mm, "end": v(-49.5, 37.5) * mm});
            skLineSegment(sketch, "E350", {"start": v(-49.5, 37.5) * mm, "end": v(-49.5, 30.5) * mm});
            skLineSegment(sketch, "E351", {"start": v(-49.5, 30.5) * mm, "end": v(-43.49, 30.5) * mm});
            skLineSegment(sketch, "E352", {"start": v(-43.49, 30.5) * mm, "end": v(-43.49, 27.5) * mm});
            skLineSegment(sketch, "E353", {"start": v(-43.49, 27.5) * mm, "end": v(-34.32, 27.5) * mm});
            skLineSegment(sketch, "E354", {"start": v(-34.32, 27.5) * mm, "end": v(-34.32, 30.5) * mm});
            skLineSegment(sketch, "E355", {"start": v(-34.32, 30.5) * mm, "end": v(-25.3, 30.5) * mm});
            skLineSegment(sketch, "E356", {"start": v(-25.3, 30.5) * mm, "end": v(-25.3, 27.5) * mm});
            skLineSegment(sketch, "E357", {"start": v(-25.3, 27.5) * mm, "end": v(-16.14, 27.5) * mm});
            skLineSegment(sketch, "E358", {"start": v(-16.14, 27.5) * mm, "end": v(-16.14, 30.5) * mm});
            skLineSegment(sketch, "E359", {"start": v(-16.14, 30.5) * mm, "end": v(-7.13, 30.5) * mm});
            skLineSegment(sketch, "E360", {"start": v(-7.13, 30.5) * mm, "end": v(-7.13, 27.5) * mm});
            skLineSegment(sketch, "E361", {"start": v(-7.13, 27.5) * mm, "end": v(2.05, 27.5) * mm});
            skLineSegment(sketch, "E362", {"start": v(2.05, 27.5) * mm, "end": v(2.05, 30.5) * mm});
            skLineSegment(sketch, "E363", {"start": v(2.05, 30.5) * mm, "end": v(11.06, 30.5) * mm});
            skLineSegment(sketch, "E364", {"start": v(11.06, 30.5) * mm, "end": v(11.06, 27.5) * mm});
            skLineSegment(sketch, "E365", {"start": v(11.06, 27.5) * mm, "end": v(20.23, 27.5) * mm});
            skLineSegment(sketch, "E366", {"start": v(20.23, 27.5) * mm, "end": v(20.23, 30.5) * mm});
            skLineSegment(sketch, "E367", {"start": v(20.23, 30.5) * mm, "end": v(29.24, 30.5) * mm});
            skLineSegment(sketch, "E368", {"start": v(29.24, 30.5) * mm, "end": v(29.24, 27.5) * mm});
            skLineSegment(sketch, "E369", {"start": v(29.24, 27.5) * mm, "end": v(38.4, 27.5) * mm});
            skLineSegment(sketch, "E370", {"start": v(38.4, 27.5) * mm, "end": v(38.4, 30.5) * mm});
            skLineSegment(sketch, "E371", {"start": v(38.4, 30.5) * mm, "end": v(44.5, 30.5) * mm});
            skLineSegment(sketch, "E372", {"start": v(44.5, 30.5) * mm, "end": v(44.5, 37.42) * mm});
            skLineSegment(sketch, "E373", {"start": v(44.5, 37.42) * mm, "end": v(47.5, 37.42) * mm});
            skLineSegment(sketch, "E374", {"start": v(47.5, 37.42) * mm, "end": v(47.5, 47.5) * mm});
            skLineSegment(sketch, "E375", {"start": v(47.5, 47.5) * mm, "end": v(44.5, 47.5) * mm});
            skLineSegment(sketch, "E376", {"start": v(44.5, 47.5) * mm, "end": v(44.5, 57.42) * mm});
            skLineSegment(sketch, "E377", {"start": v(44.5, 57.42) * mm, "end": v(47.5, 57.42) * mm});
            skLineSegment(sketch, "E378", {"start": v(47.5, 57.42) * mm, "end": v(47.5, 67.5) * mm});
            skLineSegment(sketch, "E379", {"start": v(47.5, 67.5) * mm, "end": v(44.5, 67.5) * mm});
            skLineSegment(sketch, "E380", {"start": v(44.5, 67.5) * mm, "end": v(44.5, 74.5) * mm});
            skLineSegment(sketch, "E381", {"start": v(44.5, 74.5) * mm, "end": v(38.49, 74.5) * mm});
            skLineSegment(sketch, "E382", {"start": v(38.49, 74.5) * mm, "end": v(38.49, 77.5) * mm});
            skLineSegment(sketch, "E383", {"start": v(38.49, 77.5) * mm, "end": v(29.32, 77.5) * mm});
            skLineSegment(sketch, "E384", {"start": v(29.32, 77.5) * mm, "end": v(29.32, 74.5) * mm});
            skLineSegment(sketch, "E385", {"start": v(29.32, 74.5) * mm, "end": v(20.3, 74.5) * mm});
            skLineSegment(sketch, "E386", {"start": v(20.3, 74.5) * mm, "end": v(20.3, 77.5) * mm});
            skLineSegment(sketch, "E387", {"start": v(20.3, 77.5) * mm, "end": v(11.14, 77.5) * mm});
            skLineSegment(sketch, "E388", {"start": v(11.14, 77.5) * mm, "end": v(11.14, 74.5) * mm});
            skLineSegment(sketch, "E389", {"start": v(11.14, 74.5) * mm, "end": v(2.13, 74.5) * mm});
            skLineSegment(sketch, "E390", {"start": v(2.13, 74.5) * mm, "end": v(2.13, 77.5) * mm});
            skLineSegment(sketch, "E391", {"start": v(2.13, 77.5) * mm, "end": v(-7.05, 77.5) * mm});
            skLineSegment(sketch, "E392", {"start": v(-7.05, 77.5) * mm, "end": v(-7.05, 74.5) * mm});
            skLineSegment(sketch, "E393", {"start": v(-7.05, 74.5) * mm, "end": v(-16.06, 74.5) * mm});
            skLineSegment(sketch, "E394", {"start": v(-16.06, 74.5) * mm, "end": v(-16.06, 77.5) * mm});
            skLineSegment(sketch, "E395", {"start": v(-16.06, 77.5) * mm, "end": v(-25.23, 77.5) * mm});
            skLineSegment(sketch, "E396", {"start": v(-25.23, 77.5) * mm, "end": v(-25.23, 74.5) * mm});
            skLineSegment(sketch, "E397", {"start": v(-25.23, 74.5) * mm, "end": v(-34.24, 74.5) * mm});
            skLineSegment(sketch, "E398", {"start": v(-34.24, 74.5) * mm, "end": v(-34.24, 77.5) * mm});
            skLineSegment(sketch, "E399", {"start": v(-34.24, 77.5) * mm, "end": v(-43.4, 77.5) * mm});
            skLineSegment(sketch, "E400", {"start": v(-43.4, 77.5) * mm, "end": v(-43.4, 74.5) * mm});
            skLineSegment(sketch, "E401", {"start": v(-43.4, 74.5) * mm, "end": v(-49.5, 74.5) * mm});
            skLineSegment(sketch, "E402", {"start": v(-49.5, 74.5) * mm, "end": v(-49.5, 67.58) * mm});
            skLineSegment(sketch, "E403", {"start": v(-49.5, 67.58) * mm, "end": v(-52.5, 67.58) * mm});
            skLineSegment(sketch, "E404", {"start": v(-52.5, 67.58) * mm, "end": v(-52.5, 57.5) * mm});
            skLineSegment(sketch, "E405", {"start": v(-52.5, 57.5) * mm, "end": v(-49.5, 57.5) * mm});
            skLineSegment(sketch, "E406", {"start": v(-49.5, 57.5) * mm, "end": v(-49.5, 47.58) * mm});
            skLineSegment(sketch, "E407", {"start": v(-49.5, 47.58) * mm, "end": v(-52.5, 47.58) * mm});
            skSolve(sketch);
        }
        {
            var Q0;
            Q0 = qSketchRegion(id + "F0", true);
            extrude(context, id + "F1", {"entities" : qUnion([Q0]), "depth" : 3 * mm});
        }
        {
            var Q0;
            Q0=makeQuery(id+"F0.imprint","IMPRINT",FACE,{"disambiguationData":[TD([[makeQuery(id+"F0.imprint","IMPRINT",EDGE,{"derivedFrom":sQuery(id+"F0.wireOp",EDGE,"E168")}),1.0]])]});
            extrude(context, id + "F2", {"entities" : qUnion([Q0]), "depth" : 25 * mm});
        }
        {
            var Q0;
            Q0=makeQuery(id+"F0.imprint","IMPRINT",FACE,{"disambiguationData":[TD([[makeQuery(id+"F0.imprint","IMPRINT",EDGE,{"derivedFrom":sQuery(id+"F0.wireOp",EDGE,"E288")}),1.0]])]});
            extrude(context, id + "F3", {"entities" : qUnion([Q0]), "depth" : 25 * mm});
        }
        {
            var Q0;
            Q0 = qSketchRegion(id + "F0", true);
            extrude(context, id + "F4", {"entities" : qUnion([Q0]), "depth" : 25 * mm});
        }
    });
